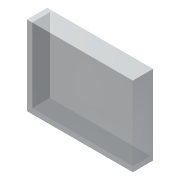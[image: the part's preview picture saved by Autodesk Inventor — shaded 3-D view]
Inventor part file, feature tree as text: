
AUTODESK INVENTOR PART (.ipt)
format: ipt  version: 2014 (Build 180170000, 170)  size: 93,184 bytes
history: native  units: mm
features: extrude x2, sketch x2
ambient origin geometry x8: Origin, YZ Plane, XZ Plane, XY Plane, X Axis, Y Axis, Z Axis, Center Point
bodies: Solid1 (feature_tree)
feature tree (4):
  extrude  "Extrusion1"  Depth=90.0mm
  extrude  "Extrusion2"  Depth=3.0mm
  sketch  "Sketch1"  dims[d0=120.0mm d1=90.0mm]
  sketch  "Sketch2"  dims[d2=3.0mm d3=0.0mm d4=3.0mm d5=3.0mm d6=20.0mm d7=0.0mm d10=120.0mm d11=40.0mm d12=60.0mm]
